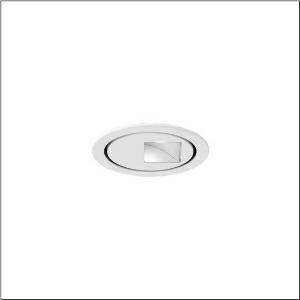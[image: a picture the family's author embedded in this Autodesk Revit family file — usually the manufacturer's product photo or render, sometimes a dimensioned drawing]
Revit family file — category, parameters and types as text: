
# Revit family: lunis_11_micro_round_51dj11b71wm21
name_source: partatom
category: Lighting Fixtures
units: mm (PartAtom-declared; Revit-internal decimal feet)

## family parameters
Cut with Voids When Loaded = No
Host = Face
Light Source = No
Part Type = Normal
Room Calculation Point = No
Round Connector Dimension = Use Diameter
Shared = No

## types (1)
- Lunis 11 micro round (1 x LED 3000K / CRI = 90 (unbekannt), 1100 lm, 3000K)
    Apparent Load = 20 VA
    CIE Flux Codes = 42 75 96 100 100
    Color Rendering = 90
    Color Temperature = 3000K
    Default Elevation = 1800 mm
    Description = Lunis 11 micro round, downlight, light control with wallwasher, of highly reflective aluminium, highly specular, light emission: direct distribution, LED rated luminous flux: 1.100lm, light colour: 930, control gear: ECG, with terminal, 3-pole, mains connection: 220..230V, AC/DC, 0/50..60Hz, LED module, luminaire module, of aluminium, highly specular, white, diameter: 114mm, clamping range: 1..40mm, recessing ring, of plastic, traffic white (RAL 9016), protection rating (complete): IP20, insulation class (complete): insulation class II (safety insulation), certification: CE, permissible ambient temperature for indoor applications: 0..+35°C, packaging unit: 1 piece
    Height = 0 mm  [stored 0 ft]
    Lamp = 1 x LED 3000K / CRI >= 90 (unbekannt)
    Lamp Light Flux = 1100 lm
    Lamp count = 1
    Length = 114 mm
    Luminous efficacy = 56 lm/W
    Manufacturer = Siteco
    ModVariant = No
    Model = 51DJ11B71WM21
    Mounting Place = Ceiling
    Mounting Type = Recessed
    Number of Poles = 1
    OnlyDefault = Yes
    Power Factor = 1
    Product Name = Lunis 11 micro round
    Product group = downlight | ceiling recessed
    ProductGroupID = 402
    Protection Class = Protection class II
    Protection Degree = IP 20
    RLX_Detail_Level = 1
    RlxData = <blob elided: 40217 chars, md5=0d3b0625>
    Socket = socket
    Standby Power = 0 W
    System Light Flux = 1100 lm
    System Power = 20 W
    Type Comments = Product without accessories
    Type Image = l_1004773.jpg
    URL = http://relux.com
    VarID = ---
    Voltage = 0 V
    Weight = 0.00 kg
    Width = 114 mm

note: [stored X ft] marks values corroborated as IEEE doubles in the binary element streams (Revit-internal decimal feet)

## geometry (parser evidence)
native form markers: Blend x4, Sweep x10
no freeform markers — native parametric forms only
